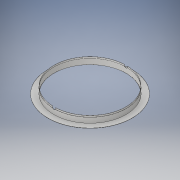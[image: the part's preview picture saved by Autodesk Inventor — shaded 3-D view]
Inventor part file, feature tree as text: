
AUTODESK INVENTOR PART (.ipt)
format: ipt  version: 2017 (Build 210142000, 142)  size: 153,600 bytes
history: native  units: in
note: dims shown in document units (in); Inventor stores cm internally (conversion verified against a paired STEP export)
features: sketch x2, revolve x1, plane x1, extrude x1
ambient origin geometry x8: Origin, YZ Plane, XZ Plane, XY Plane, X Axis, Y Axis, Z Axis, Center Point
bodies: Solid1 (feature_tree)
feature tree (5):
  revolve  "Revolution1"  [1 undecoded]
  plane  "Work Plane1"
  extrude  "Extrusion1"  Depth=0.5in
  sketch  "Sketch1"  dims[d0=1.0in d1=5.875in]
  sketch  "Sketch2"  dims[d2=1.0in d3=0.0312in d4=0.9688in d5=0.125in d6=0.25in d7=90.0deg d8=0.125in d9=0.0in d10=0.5in d11=1.0in d12=0.0in]
note: 1 required parameter value undecoded (feature->parameter linkage not recoverable at this tier; creation-order binding heuristic only, values carry confidence <= 0.55)
